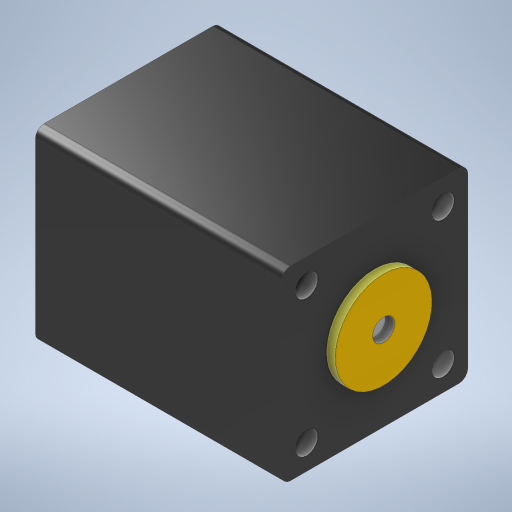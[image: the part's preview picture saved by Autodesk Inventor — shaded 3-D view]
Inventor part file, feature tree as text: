
AUTODESK INVENTOR PART (.ipt)
format: ipt  version: 2023.2 (Build 272271030, 271C)  size: 275,456 bytes
history: native  units: mm
features: extrude x3, sketch x2, plane x1, fillet x1, pattern_circular x1
ambient origin geometry x8: Origin, YZ Plane, XZ Plane, XY Plane, X Axis, Y Axis, Z Axis, Center Point
bodies: Solid1 (feature_tree)
feature tree (8):
  extrude  "Extrusion1"  Depth=42.3mm
  plane  "Work Plane1"
  sketch  "Sketch2"  dims[d2=56.0mm d3=0.0mm d4=28.0mm d5=22.0mm d6=5.0mm d7=2.0mm d8=0.0mm d11=2.0mm d12=40.0mm d13=360.0deg d15=5.1mm d16=31.0mm d17=31.0mm d18=0.0mm d19=0.0mm d20=1.0mm]
  extrude  "Extrusion2"  Depth=28.0mm
  fillet  "Fillet1"  Radius=22.0mm
  pattern_circular  "Circular Pattern1"  [2 undecoded]
  extrude  "Extrusion4"  Depth=2.0mm TaperAngle=0.0deg
  sketch  "Sketch1"  dims[d0=42.3mm d1=42.3mm]
note: 2 required parameter values undecoded (feature->parameter linkage not recoverable at this tier; creation-order binding heuristic only, values carry confidence <= 0.55)
